# Revit family: Bottle_Filler_Fountain-Sloan-Valve-DRS120z
name_source: partatom
category: Plumbing Fixtures
units: mm (PartAtom-declared; Revit-internal decimal feet)

## family parameters
Cut with Voids When Loaded = No
Host = Face
OmniClass Number = 23.45.05.00
OmniClass Title = Sanitary Equipment
Part Type = Normal
Room Calculation Point = No
Round Connector Dimension = Use Diameter
Shared = No

## types (4) — shared parameters
ADA Compliant = Yes
Apparent Load = 240 VA
Assembly Code = D2010810
CW Connection = Yes
CWFU = 1.2
Cold Water Connection Diameter = 3/8"
Cold Water Connector Description = Cold Water Connector
Connector Description = Electrical Connection
Current = 5 A
Default Elevation = 0"
Depth = 19 1/16"
Frequency = 60 Hz
HW Connection = No
Height = 38 9/32"
Manufacturer = Sloan Valve
Number of Poles = 3
Power Factor = 0.8
Refrigeration option = Yes
Sanitary Drain Connection Diameter = 1 1/4"
Sanitary Drain Connector Description = Sanitary Drain Connector
URL = www.sloanvalve.com
Vent Connection = No
Version = 1
Voltage = 115 V
WFU = 2
Waste Connection = Yes
Water Flow = 1.2 GPM
Weight = 110.00 lb
Width = 38"
zero-valued in all types: HWFU

## per-type parameters (varying)
| type | Description | Filter option | Model | Part Number | Product Material |
| DRS120-FIL-REF-BLK - Refrigerated and Filtered | Sloan DropSpot™ on-wall bottle filler with bi-level cooler, filtered, refrigerated black powder coat | Yes | DRS120-FIL-REF-BLK | 33820030 | Sloan Valve - Finish - Black Powder Coat |
| DRS120-FIL-REF-SS - Refrigerated and Filtered | Sloan DropSpot™ on-wall bottle filler with bi-level cooler, filtered, refrigerated stainless | Yes | DRS120-FIL-REF-SS | 33820006 | Sloan Valve - Finish - Stainless Steel |
| DRS120-UNFIL-REF-SS - Refrigerated | Sloan DropSpot™ on-wall bottle filler with bi-level cooler, unfiltered, refrigerated stainless | No | DRS120-UNFIL-REF-SS | 33820003 | Sloan Valve - Finish - Stainless Steel |
| DRS120-UNFIL-REF-BLK - Refrigerated | Sloan DropSpot™ on-wall bottle filler with bi-level cooler, unfiltered, refrigerated black powder coat | No | DRS120-UNFIL-REF-BLK | 33820027 | Sloan Valve - Finish - Black Powder Coat |

## geometry (parser evidence)
native form markers: Sweep x4
no freeform markers — native parametric forms only
